# Revit family: Paradise_CWS_Paper universal
name_source: partatom
category: Plumbing Fixtures
revit_build: Autodesk Revit Architecture 2014 (Build: 20130308_1515(x64)
units: mm (PartAtom-declared; Revit-internal decimal feet)

## types (1)
- Plastic-CWS-Paradise Paper Universal-White
    BIMobject category = Dispensers
    Date of publishing = 2015-09-17
    Depth = 140 mm
    Description = Paradise Paper Universal folded paper dispenser for approx. 600 folded papers. Housing made of impact-proof, anti-static plastic, with lock. Rounded edges ensure no risk of injury. Comes complete with fastening materials, delivery and installation.

Dispenser & panel:
Dispenser with panel white : 4620000

Folded paper:
various paper types in different qualities and colours
    Design country = Germany
    EAN code = 4049657013441
    Edition number = 1
    Height = 579 mm
    IFC Classification = Furniture
    Installation instructions = http://www.cws-boco.de
    Logo Material = Logo-CWS-Paradise Paper Universal-Red
    Manufacturer URL = http://cws-boco.ie
    Manufacturer country = Switzerland
    Manufacturer name = CWS-boco
    Material main = Plastic-CWS-Paradise Paper Universal-White
    NBS Reference Code = 31-76
    NBS Reference Description = Sanitary Dispensing And Disposal Units
    Nominal height = 579
    Nominal width = 299
    Product Guid = e0cbd8af-e668-43b7-b32f-01acbe8fce60
    Product SKU = 4620000
    Product certification = http://www.cws-boco.de
    Product data url = http://bimobject.com
    Product family = CWS ParadiseLine
    Product group = Folded paper dispenser
    QR code = http://bimobject.com
    UNSPSC Code = 301815
    UNSPSC name = Sanitary ware
    URL = http://cws-boco.ie
    Uniclass 1.4 Code = JN13
    Uniclass 1.4 Description = Sanitary appliances/fittings
    Uniclass 2.0 Code = PR-31-76
    Uniclass 2.0 Description = Sanitary Dispensing And Disposal Units
    Weight Net (Kg) = 2.03
    Width = 299 mm
    Youtube clip = https://www.youtube.com

## geometry (parser evidence)
native form markers: Sweep x5
no freeform markers — native parametric forms only
